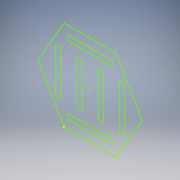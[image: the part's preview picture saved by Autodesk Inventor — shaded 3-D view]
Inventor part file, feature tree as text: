
AUTODESK INVENTOR PART (.ipt)
format: ipt  version: 2019 (Build 230136000, 136)  size: 93,696 bytes
history: native  units: mm
features: sketch x1
ambient origin geometry x8: Origin, YZ Plane, XZ Plane, XY Plane, X Axis, Y Axis, Z Axis, Center Point
feature tree (1):
  sketch  "Sketch1"
